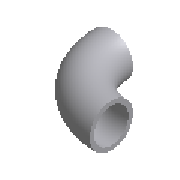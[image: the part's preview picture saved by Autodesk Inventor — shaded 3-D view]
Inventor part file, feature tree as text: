
AUTODESK INVENTOR PART (.ipt)
format: ipt  version: 2025.1 (Build 291241020, 241B)  size: 186,368 bytes
history: native  units: mm (DEFAULTED — no unit token found)
features: other x4, sweep x1
ambient origin geometry x8: Origin, YZ Plane, XZ Plane, XY Plane, X Axis, Y Axis, Z Axis, Center Point
bodies: Solid1 (feature_tree)
feature tree (5):
  sweep  "Sweep1"
  other  "Work Point1"
  other  "Work Point2"
  other  "Work Axis1"
  other  "Work Axis2"
